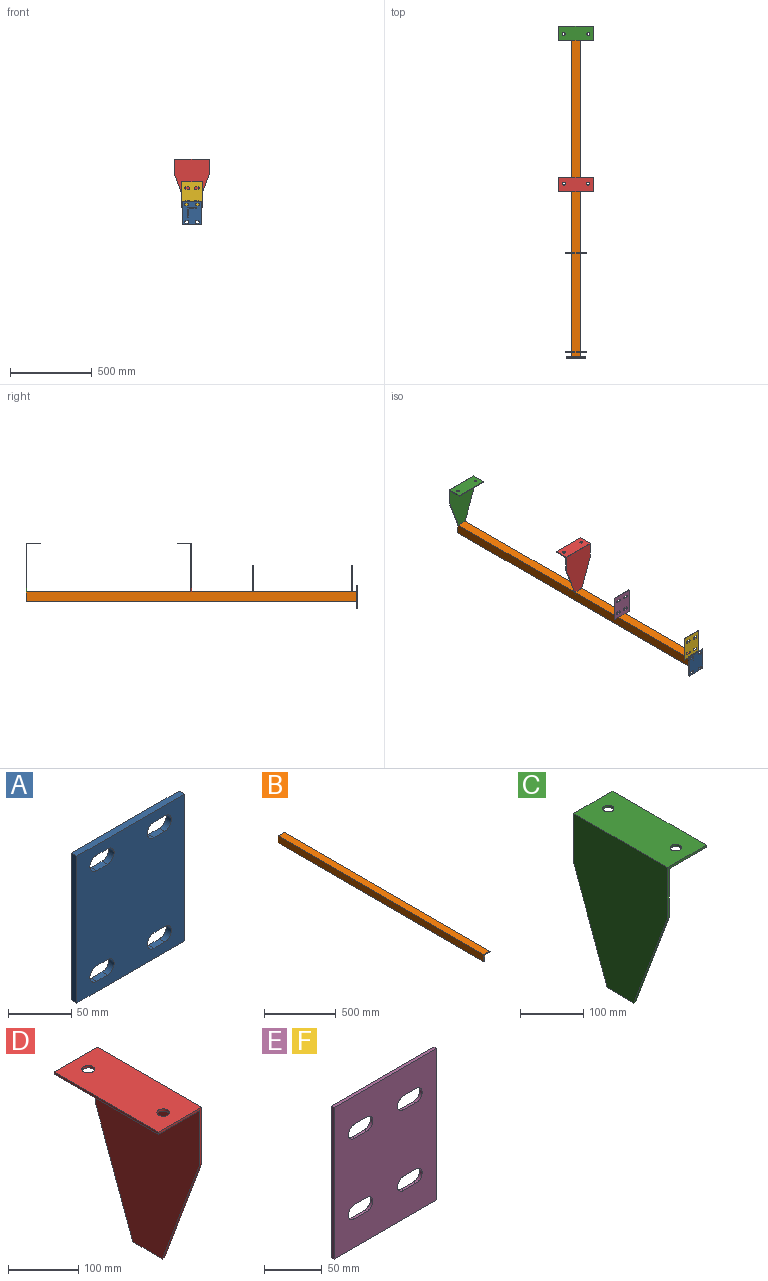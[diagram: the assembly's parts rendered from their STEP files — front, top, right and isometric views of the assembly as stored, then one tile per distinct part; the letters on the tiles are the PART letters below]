
ASSEMBLY  parts=6 mates=5
PART A: 22 faces, bbox 120x6x142 mm
  f0: cylinder r=7.5mm len=15mm, axis (0,1,0), area 141.4mm2, adj f1,f19,f20,f21
  f1: plane 12x6mm, normal (0,0,-1), area 72mm2, adj f0,f2,f20,f21
  f2: cylinder r=7.5mm len=15mm, axis (0,1,0), area 141.4mm2, adj f1,f19,f20,f21
  f3: cylinder r=7.5mm len=15mm, axis (0,1,0), area 141.4mm2, adj f4,f15,f20,f21
  f4: plane 12x6mm, normal (0,0,1), area 72mm2, adj f3,f5,f20,f21
  f5: cylinder r=7.5mm len=15mm, axis (0,1,0), area 141.4mm2, adj f4,f15,f20,f21
  f6: plane 12x6mm, normal (0,0,-1), area 72mm2, adj f7,f16,f20,f21
  f7: cylinder r=7.5mm len=15mm, axis (0,1,0), area 141.4mm2, adj f6,f8,f20,f21
  f8: plane 12x6mm, normal (0,0,1), area 72mm2, adj f7,f16,f20,f21
  f9: plane 12x6mm, normal (0,0,1), area 72mm2, adj f10,f17,f20,f21
  f10: cylinder r=7.5mm len=15mm, axis (0,1,0), area 141.4mm2, adj f9,f11,f20,f21
  f11: plane 12x6mm, normal (0,0,-1), area 72mm2, adj f10,f17,f20,f21
  f12: plane 142x6mm, normal (1,0,0), area 852mm2, adj f13,f18,f20,f21
  f13: plane 120x6mm, normal (0,0,1), area 720mm2, adj f12,f14,f20,f21
  f14: plane 142x6mm, normal (-1,0,0), area 852mm2, adj f13,f18,f20,f21
  f15: plane 12x6mm, normal (0,0,-1), area 72mm2, adj f3,f5,f20,f21
  f16: cylinder r=7.5mm len=15mm, axis (0,1,0), area 141.4mm2, adj f6,f8,f20,f21
  f17: cylinder r=7.5mm len=15mm, axis (0,1,0), area 141.4mm2, adj f9,f11,f20,f21
  f18: plane 120x6mm, normal (0,0,-1), area 720mm2, adj f12,f14,f20,f21
  f19: plane 12x6mm, normal (0,0,1), area 72mm2, adj f0,f2,f20,f21
  f20: plane 142x120mm, normal (0,-1,0), area 15613.1mm2, adj f0,f1,f2,f3,f4,f5,f6,f7
  f21: plane 142x120mm, normal (0,1,0), area 15613.1mm2, adj f0,f1,f2,f3,f4,f5,f6,f7
PART B: 11 faces, bbox 60x2030x60 mm
  f0: plane 2030x42mm, normal (1,0,0), area 85260mm2, adj f6,f7,f8,f10
  f1: plane 2030x42mm, normal (0,0,-1), area 85260mm2, adj f6,f7,f8,f9
  f2: plane 2030x2mm, normal (1,0,0), area 4060mm2, adj f3,f6,f7,f9
  f3: plane 2030x60mm, normal (0,0,1), area 121800mm2, adj f2,f4,f6,f7
  f4: plane 2030x60mm, normal (-1,0,0), area 121800mm2, adj f3,f5,f6,f7
  f5: plane 2030x2mm, normal (0,0,-1), area 4060mm2, adj f4,f6,f7,f10
  f6: plane 60x60mm, normal (0,-1,0), area 690.9mm2, adj f0,f1,f2,f3,f4,f5,f8,f9
  f7: plane 60x60mm, normal (0,1,0), area 690.9mm2, adj f0,f1,f2,f3,f4,f5,f8,f9
  f8: cylinder r=8mm len=2030mm, axis (0,-1,0), area 25509.7mm2, adj f0,f1,f6,f7
  f9: cylinder r=4mm len=2030mm, axis (0,1,0), area 12754.9mm2, adj f1,f2,f6,f7
  f10: cylinder r=4mm len=2030mm, axis (0,1,0), area 12754.9mm2, adj f0,f5,f6,f7
PART C: 12 faces, bbox 87x210x300 mm
  f0: plane 60x4mm, normal (0,0,-1), area 240mm2, adj f1,f2,f10,f11
  f1: plane 300x210mm, normal (-1,0,0), area 47761.3mm2, adj f0,f3,f4,f6,f10,f11
  f2: plane 296x210mm, normal (1,0,0), area 46921.3mm2, adj f0,f3,f4,f7,f10,f11
  f3: plane 98.26x87mm, normal (0,-1,0), area 725mm2, adj f1,f2,f5,f6,f7,f10
  f4: plane 95.38x87mm, normal (0,1,0), area 713.5mm2, adj f1,f2,f5,f6,f7,f11
  f5: plane 210x4mm, normal (1,0,0), area 840mm2, adj f3,f4,f6,f7
  f6: plane 210x87mm, normal (0,0,1), area 17761.1mm2, adj f1,f3,f4,f5,f8,f9
  f7: plane 210x83mm, normal (0,0,-1), area 16921.1mm2, adj f2,f3,f4,f5,f8,f9
  f8: cylinder r=9mm len=18mm, axis (0,0,1), area 226.2mm2, adj f6,f7
  f9: cylinder r=9mm len=18mm, axis (0,0,1), area 226.2mm2, adj f6,f7
  f10: plane 201.74x75mm, normal (0,-0.94,-0.35), area 860.9mm2, adj f0,f1,f2,f3
  f11: plane 204.62x75mm, normal (0,0.94,-0.34), area 871.7mm2, adj f0,f1,f2,f4
PART D: 12 faces, bbox 87x210x300 mm
  f0: plane 300x210mm, normal (1,0,0), area 47761.3mm2, adj f1,f3,f4,f6,f10,f11
  f1: plane 60x4mm, normal (0,0,-1), area 240mm2, adj f0,f2,f10,f11
  f2: plane 296x210mm, normal (-1,0,0), area 46921.3mm2, adj f1,f3,f4,f7,f10,f11
  f3: plane 98.26x87mm, normal (0,-1,0), area 725mm2, adj f0,f2,f5,f6,f7,f10
  f4: plane 95.38x87mm, normal (0,1,0), area 713.5mm2, adj f0,f2,f5,f6,f7,f11
  f5: plane 210x4mm, normal (-1,0,0), area 840mm2, adj f3,f4,f6,f7
  f6: plane 210x87mm, normal (0,0,1), area 17761.1mm2, adj f0,f3,f4,f5,f8,f9
  f7: plane 210x83mm, normal (0,0,-1), area 16921.1mm2, adj f2,f3,f4,f5,f8,f9
  f8: cylinder r=9mm len=18mm, axis (0,0,1), area 226.2mm2, adj f6,f7
  f9: cylinder r=9mm len=18mm, axis (0,0,1), area 226.2mm2, adj f6,f7
  f10: plane 201.74x75mm, normal (0,-0.94,-0.35), area 860.9mm2, adj f0,f1,f2,f3
  f11: plane 204.62x75mm, normal (0,0.94,-0.34), area 871.7mm2, adj f0,f1,f2,f4
PART E: 22 faces, bbox 125x3x160 mm
  f0: cylinder r=7.5mm len=15mm, axis (0,1,0), area 70.7mm2, adj f1,f19,f20,f21
  f1: plane 15x3mm, normal (0,0,-1), area 45mm2, adj f0,f2,f20,f21
  f2: cylinder r=7.5mm len=15mm, axis (0,1,0), area 70.7mm2, adj f1,f19,f20,f21
  f3: cylinder r=7.5mm len=15mm, axis (0,1,0), area 70.7mm2, adj f4,f15,f20,f21
  f4: plane 15x3mm, normal (0,0,-1), area 45mm2, adj f3,f5,f20,f21
  f5: cylinder r=7.5mm len=15mm, axis (0,1,0), area 70.7mm2, adj f4,f15,f20,f21
  f6: plane 15x3mm, normal (0,0,-1), area 45mm2, adj f7,f16,f20,f21
  f7: cylinder r=7.5mm len=15mm, axis (0,1,0), area 70.7mm2, adj f6,f8,f20,f21
  f8: plane 15x3mm, normal (0,0,1), area 45mm2, adj f7,f16,f20,f21
  f9: plane 15x3mm, normal (0,0,1), area 45mm2, adj f10,f17,f20,f21
  f10: cylinder r=7.5mm len=15mm, axis (0,1,0), area 70.7mm2, adj f9,f11,f20,f21
  f11: plane 15x3mm, normal (0,0,-1), area 45mm2, adj f10,f17,f20,f21
  f12: plane 160x3mm, normal (1,0,0), area 480mm2, adj f13,f18,f20,f21
  f13: plane 125x3mm, normal (0,0,1), area 375mm2, adj f12,f14,f20,f21
  f14: plane 160x3mm, normal (-1,0,0), area 480mm2, adj f13,f18,f20,f21
  f15: plane 15x3mm, normal (0,0,1), area 45mm2, adj f3,f5,f20,f21
  f16: cylinder r=7.5mm len=15mm, axis (0,1,0), area 70.7mm2, adj f6,f8,f20,f21
  f17: cylinder r=7.5mm len=15mm, axis (0,1,0), area 70.7mm2, adj f9,f11,f20,f21
  f18: plane 125x3mm, normal (0,0,-1), area 375mm2, adj f12,f14,f20,f21
  f19: plane 15x3mm, normal (0,0,1), area 45mm2, adj f0,f2,f20,f21
  f20: plane 160x125mm, normal (0,-1,0), area 18393.1mm2, adj f0,f1,f2,f3,f4,f5,f6,f7
  f21: plane 160x125mm, normal (0,1,0), area 18393.1mm2, adj f0,f1,f2,f3,f4,f5,f6,f7
PART F: same geometry as E
PLACE A t=(-8.75,2.47,6.78)mm
PLACE B t=(14.49,1017.47,15.16)mm
PLACE C rot(axis=(0,0,-1),90deg) t=(-8.75,1898.85,176.33)mm
PLACE D rot(axis=(0,0,-1),90deg) t=(-8.75,1057.85,176.33)mm
PLACE E t=(-8.75,641.47,119.78)mm
PLACE F t=(-8.75,35.47,119.78)mm
MATE fastened B.f6 <-> A.f21  axis (0,-1,0) through (-8.75,2.47,39.78)mm
MATE fastened D.f1 <-> B.f3  axis (0,0,-1) through (-8.75,1017.47,39.78)mm
MATE fastened F.f18 <-> B.f3  axis (0,0,-1) through (-8.75,32.47,39.78)mm
MATE fastened E.f18 <-> B.f3  axis (0,0,-1) through (-8.75,638.47,39.78)mm
MATE fastened C.f0 <-> B.f3  axis (0,0,-1) through (-8.75,2032.47,39.78)mm
